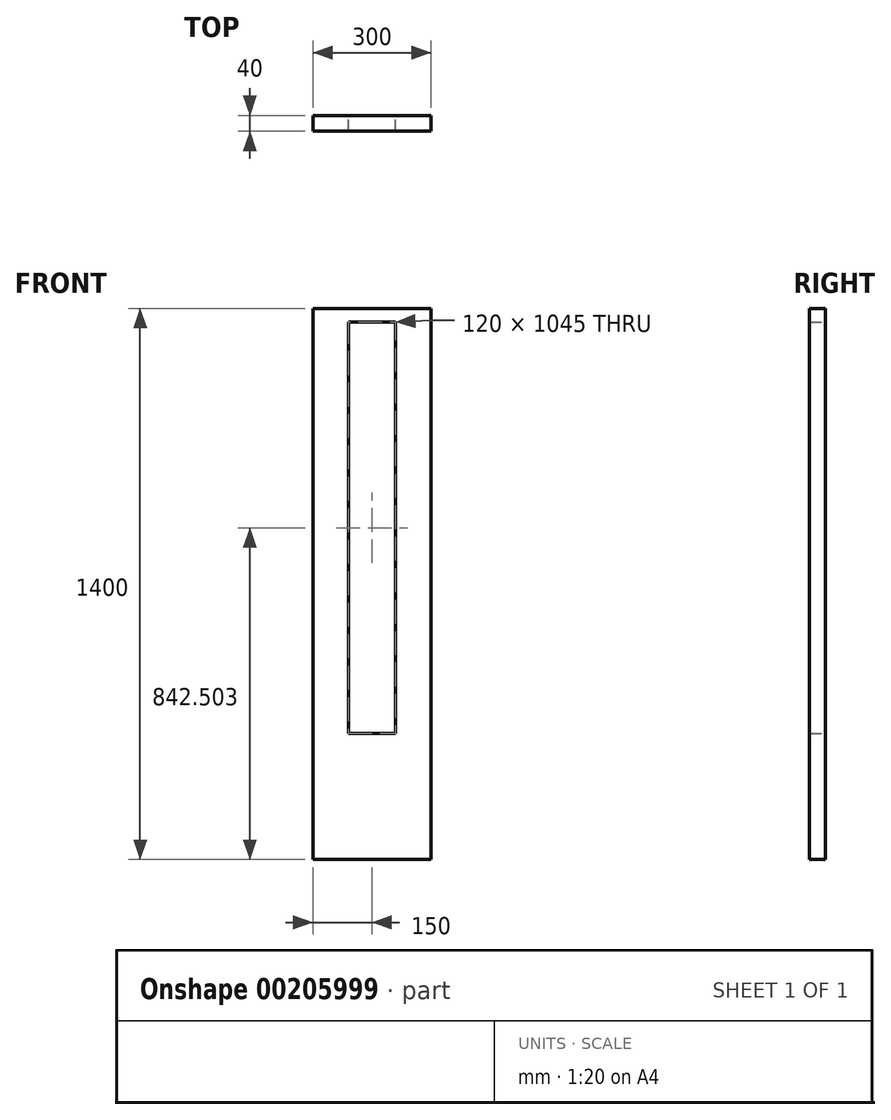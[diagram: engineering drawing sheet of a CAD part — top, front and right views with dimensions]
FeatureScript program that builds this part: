
annotation { "Feature Type Name" : "Feature", "Feature Type Description" : "" }
export const myFeature = defineFeature(function(context is Context, id is Id, definition is map)
    precondition{}
    {
        {
            var Q0;
            Q0=qCreatedBy(makeId("Front.planeOp"),FACE);
            var sketch = newSketch(context, id + "F0", { "sketchPlane" : qUnion([Q0])});
            skLineSegment(sketch, "E0.bottom", {"start": v(-150, 583.7) * mm, "end": v(0, 583.7) * mm});
            skLineSegment(sketch, "E0.left", {"start": v(-150, 583.7) * mm, "end": v(-150, -816.3) * mm});
            skLineSegment(sketch, "E1.MirrorCS", {"start": v(150, 583.7) * mm, "end": v(150, -816.3) * mm});
            skLineSegment(sketch, "E2.MirrorCS", {"start": v(171.25, 583.7) * mm, "end": v(21.25, 583.7) * mm});
            skLineSegment(sketch, "E3", {"start": v(0, 583.7) * mm, "end": v(50, 583.7) * mm});
            skLineSegment(sketch, "E4", {"start": v(0, 548.7) * mm, "end": v(-60, 548.7) * mm});
            skLineSegment(sketch, "E5", {"start": v(-60, 548.7) * mm, "end": v(-60, -496.3) * mm});
            skLineSegment(sketch, "E6.MirrorCS", {"start": v(0, 548.7) * mm, "end": v(60, 548.7) * mm});
            skLineSegment(sketch, "E7.MirrorCS", {"start": v(60, 519.45) * mm, "end": v(60, -496.3) * mm});
            skLineSegment(sketch, "E8", {"start": v(-60, -496.3) * mm, "end": v(60, -496.3) * mm});
            skLineSegment(sketch, "E9", {"start": v(-150, -816.3) * mm, "end": v(150, -816.3) * mm});
            skLineSegment(sketch, "E10.top", {"start": v(-60, -441.3) * mm, "end": v(60, -441.3) * mm});
            skLineSegment(sketch, "E10.left", {"start": v(-60, -496.3) * mm, "end": v(-60, -441.3) * mm});
            skLineSegment(sketch, "E10.right", {"start": v(60, -496.3) * mm, "end": v(60, -441.3) * mm});
            skLineSegment(sketch, "E11", {"start": v(60, 548.7) * mm, "end": v(60, 519.45) * mm});
            skSolve(sketch);
        }
        {
            var Q0;
            {var subQ0=sQuery(id+"F0.wireOp",EDGE,"E0.bottom");Q0=makeQuery(id+"F0.imprint","IMPRINT",FACE,{"disambiguationData":[TD([[makeQuery(id+"F0.imprint","IMPRINT",EDGE,{"derivedFrom":subQ0}),-1.0]])]});}
            extrude(context, id + "F1", {"entities" : qUnion([Q0]), "depth" : 40 * mm});
        }
    });
